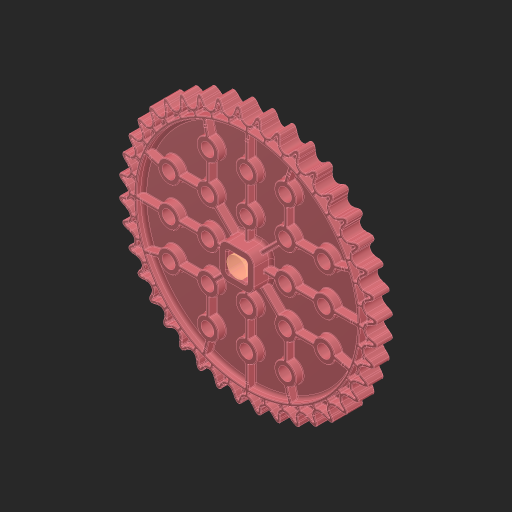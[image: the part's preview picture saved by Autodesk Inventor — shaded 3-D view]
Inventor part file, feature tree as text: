
AUTODESK INVENTOR PART (.ipt)
format: ipt  version: 2023 (Build 270158000, 158)  size: 12,610,048 bytes
history: native  units: in
note: dims shown in document units (in); Inventor stores cm internally (conversion verified against a paired STEP export)
features: sketch x1, other x1, mirror x1, extrude x1
ambient origin geometry x8: Origin, YZ Plane, XZ Plane, XY Plane, X Axis, Y Axis, Z Axis, Center Point
bodies: Solid1 (feature_tree)
feature tree (4):
  sketch  "Sketch1"  dims[d0=0.25in d1=0.3937in d2=0.0in]
  other  "Srf1"
  mirror  "Mirror1"
  extrude  "ExtrusionSrf1"  Depth=0.3937in TaperAngle=0.0deg
